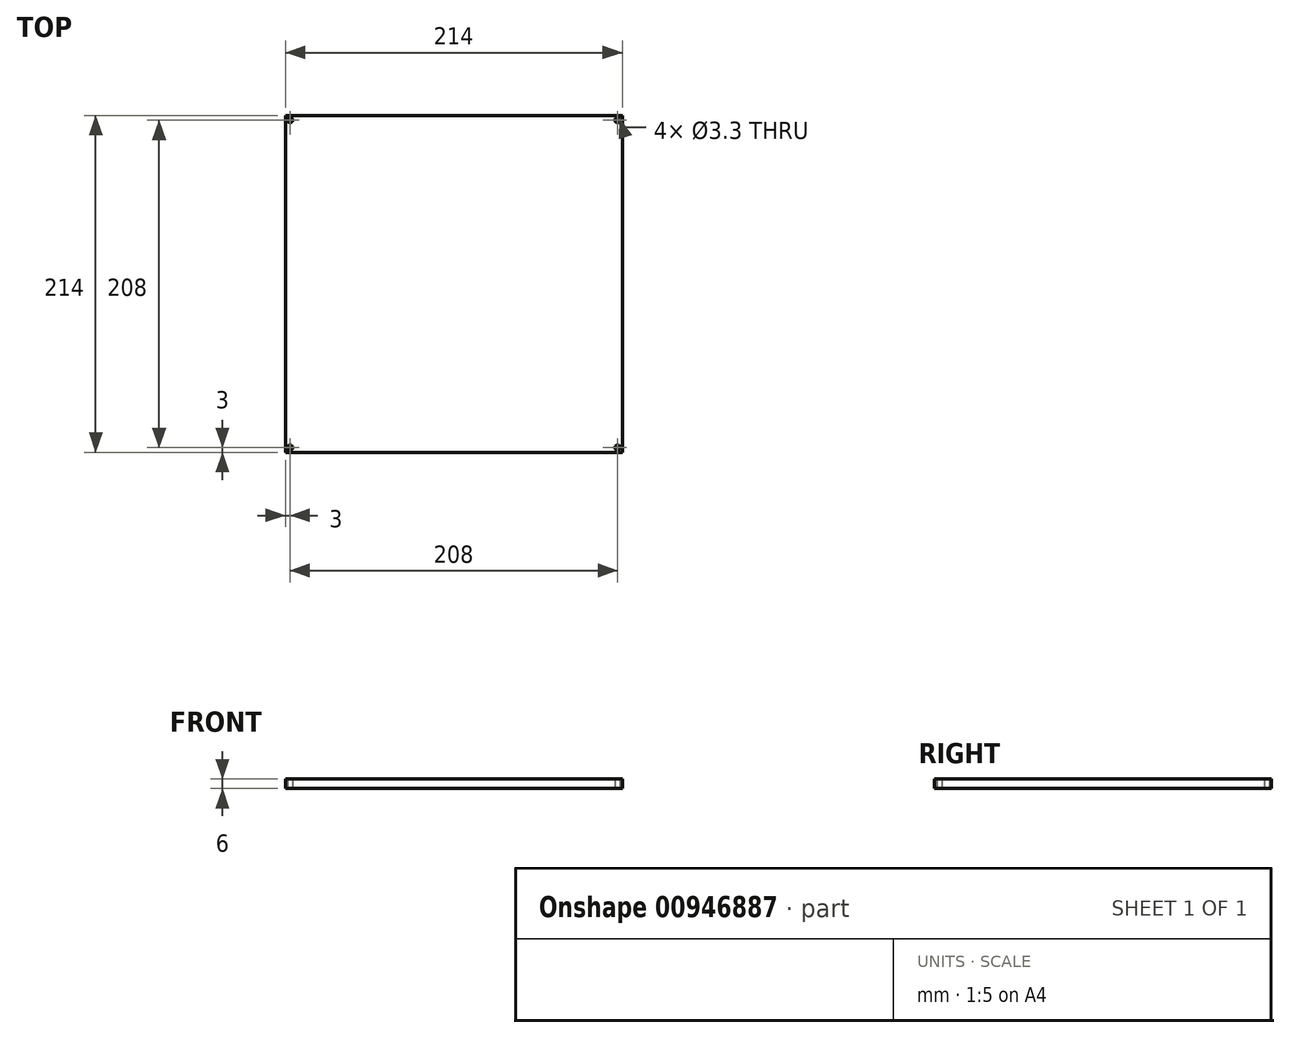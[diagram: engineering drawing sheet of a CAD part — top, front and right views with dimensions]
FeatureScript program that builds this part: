
annotation { "Feature Type Name" : "Feature", "Feature Type Description" : "" }
export const myFeature = defineFeature(function(context is Context, id is Id, definition is map)
    precondition{}
    {
        {
            var Q0;
            Q0=qCreatedBy(makeId("Top.planeOp"),FACE);
            var sketch = newSketch(context, id + "F0", { "sketchPlane" : qUnion([Q0])});
            skLineSegment(sketch, "E0.bottom", {"start": v(0, 0) * mm, "end": v(214, 0) * mm});
            skLineSegment(sketch, "E0.top", {"start": v(0, 214) * mm, "end": v(214, 214) * mm});
            skLineSegment(sketch, "E0.left", {"start": v(0, 0) * mm, "end": v(0, 214) * mm});
            skLineSegment(sketch, "E0.right", {"start": v(214, 0) * mm, "end": v(214, 214) * mm});
            skCircle(sketch, "E1", {"center": v(3, 211) * mm, "radius": 1.65 * mm});
            skCircle(sketch, "E2", {"center": v(211, 211) * mm, "radius": 1.65 * mm});
            skCircle(sketch, "E3", {"center": v(211, 3) * mm, "radius": 1.65 * mm});
            skCircle(sketch, "E4", {"center": v(3, 3) * mm, "radius": 1.65 * mm});
            skLineSegment(sketch, "E5", {"start": v(3, 211) * mm, "end": v(3, 214) * mm, "construction": true});
            skLineSegment(sketch, "E6", {"start": v(3, 211) * mm, "end": v(0, 211) * mm, "construction": true});
            skLineSegment(sketch, "E7", {"start": v(211, 211) * mm, "end": v(211, 214) * mm, "construction": true});
            skLineSegment(sketch, "E8", {"start": v(211, 211) * mm, "end": v(214, 211) * mm, "construction": true});
            skLineSegment(sketch, "E9", {"start": v(211, 3) * mm, "end": v(214, 3) * mm, "construction": true});
            skLineSegment(sketch, "E10", {"start": v(211, 3) * mm, "end": v(211, 0) * mm, "construction": true});
            skLineSegment(sketch, "E11", {"start": v(3, 3) * mm, "end": v(0, 3) * mm, "construction": true});
            skLineSegment(sketch, "E12", {"start": v(3, 3) * mm, "end": v(3, 0) * mm, "construction": true});
            skSolve(sketch);
        }
        {
            var Q0;
            Q0 = qSketchRegion(id + "F0", true);
            extrude(context, id + "F1", {"entities" : qUnion([Q0]), "depth" : 6 * mm, "offsetDistance" : 25 * mm});
        }
    });
